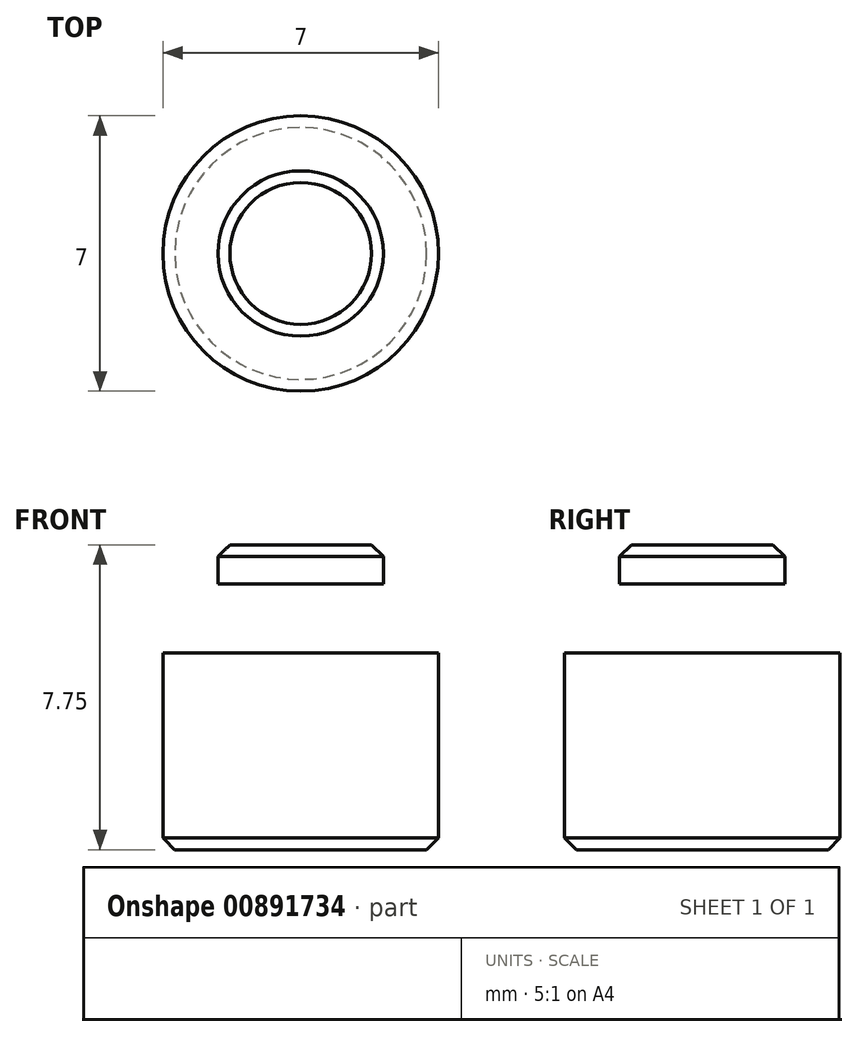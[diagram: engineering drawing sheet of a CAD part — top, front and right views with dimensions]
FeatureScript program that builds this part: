
annotation { "Feature Type Name" : "Feature", "Feature Type Description" : "" }
export const myFeature = defineFeature(function(context is Context, id is Id, definition is map)
    precondition{}
    {
        {
            var Q0;
            Q0=qCreatedBy(makeId("Front.planeOp"),FACE);
            var sketch = newSketch(context, id + "F0", { "sketchPlane" : qUnion([Q0])});
            skLineSegment(sketch, "E0.bottom", {"start": v(0, 0) * mm, "end": v(3.5, 0) * mm});
            skLineSegment(sketch, "E0.top", {"start": v(0, 5) * mm, "end": v(3.5, 5) * mm});
            skLineSegment(sketch, "E0.left", {"start": v(0, 0) * mm, "end": v(0, 5) * mm});
            skLineSegment(sketch, "E0.right", {"start": v(3.5, 0) * mm, "end": v(3.5, 5) * mm});
            skLineSegment(sketch, "E1.bottom", {"start": v(0, 5) * mm, "end": v(2, 5) * mm});
            skLineSegment(sketch, "E1.top", {"start": v(0, 6.75) * mm, "end": v(2, 6.75) * mm});
            skLineSegment(sketch, "E1.left", {"start": v(0, 5) * mm, "end": v(0, 6.75) * mm});
            skLineSegment(sketch, "E1.right", {"start": v(2, 5) * mm, "end": v(2, 6.75) * mm});
            skLineSegment(sketch, "E2.bottom", {"start": v(0, 6.75) * mm, "end": v(2.1, 6.75) * mm});
            skLineSegment(sketch, "E2.top", {"start": v(0, 7.75) * mm, "end": v(2.1, 7.75) * mm});
            skLineSegment(sketch, "E2.left", {"start": v(0, 6.75) * mm, "end": v(0, 7.75) * mm});
            skLineSegment(sketch, "E2.right", {"start": v(2.1, 6.75) * mm, "end": v(2.1, 7.75) * mm});
            skSolve(sketch);
        }
        {
            var Q0;
            Q0=makeQuery(id+"F0.imprint","IMPRINT",FACE,{"disambiguationData":[TD([[makeQuery(id+"F0.imprint","IMPRINT",EDGE,{"derivedFrom":sQuery(id+"F0.wireOp",EDGE,"E0.bottom")}),1.0]])]});
            var Q1;
            Q1=makeQuery(id+"F0.imprint","IMPRINT",FACE,{"disambiguationData":[TD([[makeQuery(id+"F0.imprint","IMPRINT",EDGE,{"derivedFrom":sQuery(id+"F0.wireOp",EDGE,"E1.bottom")}),1.0]])]});
            var Q2;
            Q2=makeQuery(id+"F0.imprint","IMPRINT",FACE,{"disambiguationData":[TD([[makeQuery(id+"F0.imprint","IMPRINT",EDGE,{"derivedFrom":sQuery(id+"F0.wireOp",EDGE,"E2.top")}),-1.0]])]});
            var Q3;
            Q3=sQuery(id+"F0.wireOp",EDGE,"E0.left");
            revolve(context, id + "F1", {"surfaceOperationType" : NewSurfaceOperationType.NEW, "entities" : qUnion([Q0, Q1, Q2]), "axis" : qUnion([Q3]), "revolveType" : RevolveType.FULL});
        }
        {
            var Q0;
            Q0=makeQuery(id+"F1.opRevolve","SWEPT_EDGE",EDGE,{"disambiguationData":[OSD([sQuery(id+"F0.wireOp",EDGE,"E2.top"),sQuery(id+"F0.wireOp",EDGE,"E2.right")])]});
            var Q1;
            Q1=makeQuery(id+"F1.opRevolve","SWEPT_EDGE",EDGE,{"disambiguationData":[OSD([sQuery(id+"F0.wireOp",EDGE,"E0.bottom"),sQuery(id+"F0.wireOp",EDGE,"E0.right")])]});
            chamfer(context, id + "F2", {"entities" : qUnion([Q0, Q1]), "width" : .3 * mm, "tangentPropagation" : true});
        }
    });
